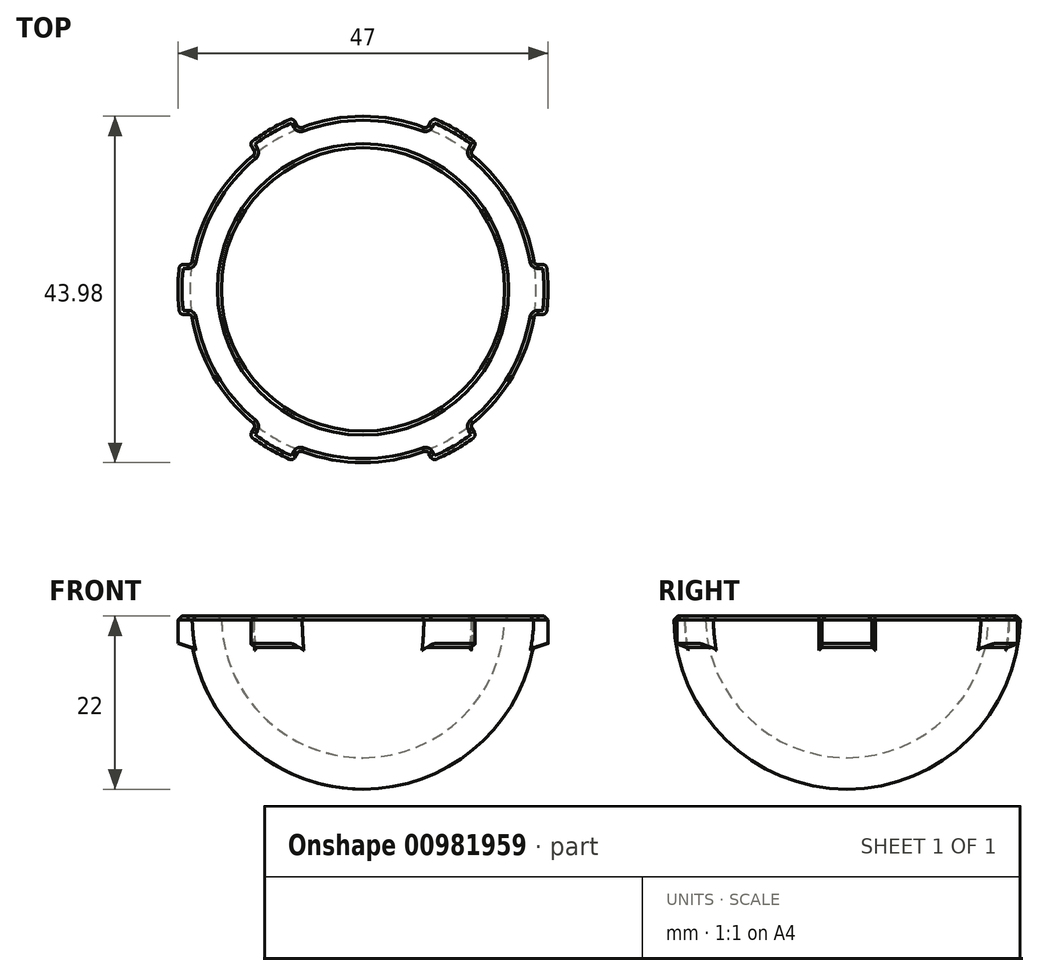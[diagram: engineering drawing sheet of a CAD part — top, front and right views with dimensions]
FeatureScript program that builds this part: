
annotation { "Feature Type Name" : "Feature", "Feature Type Description" : "" }
export const myFeature = defineFeature(function(context is Context, id is Id, definition is map)
    precondition{}
    {
        {
            var Q0;
            Q0=qCreatedBy(makeId("Front.planeOp"),FACE);
            var sketch = newSketch(context, id + "F0", { "sketchPlane" : qUnion([Q0])});
            skArc(sketch, "E0", {"start": v(-22, 0) * mm, "mid": v(-15.56, -15.56) * mm, "end": v(0, -22) * mm});
            skLineSegment(sketch, "E1", {"start": v(0, -22) * mm, "end": v(0, -18) * mm});
            skArc(sketch, "E2", {"start": v(0, -18) * mm, "mid": v(-12.73, -12.73) * mm, "end": v(-18, 0) * mm});
            skLineSegment(sketch, "E3", {"start": v(-22, 0) * mm, "end": v(-18, 0) * mm});
            skSolve(sketch);
        }
        {
            var Q0;
            Q0=makeQuery(id+"F0.imprint","IMPRINT",FACE,{"disambiguationData":[TD([[makeQuery(id+"F0.imprint","IMPRINT",EDGE,{"derivedFrom":sQuery(id+"F0.wireOp",EDGE,"E0")}),1.0]])]});
            var Q1;
            Q1=sQuery(id+"F0.wireOp",EDGE,"E1");
            revolve(context, id + "F1", {"surfaceOperationType" : NewSurfaceOperationType.NEW, "entities" : qUnion([Q0]), "axis" : qUnion([Q1]), "revolveType" : RevolveType.FULL});
        }
        {
            var Q0;
            Q0=qCreatedBy(makeId("Top.planeOp"),FACE);
            var sketch = newSketch(context, id + "F2", { "sketchPlane" : qUnion([Q0])});
            skArc(sketch, "E4", {"start": v(23.28, 3.17) * mm, "mid": v(23.5, 0) * mm, "end": v(23.28, -3.18) * mm});
            skLineSegment(sketch, "E5", {"start": v(23.28, -3.18) * mm, "end": v(18, -3.18) * mm});
            skLineSegment(sketch, "E6", {"start": v(23.28, 3.17) * mm, "end": v(18, 3.17) * mm});
            skLineSegment(sketch, "E7", {"start": v(18, 3.17) * mm, "end": v(18, -3.18) * mm});
            skSolve(sketch);
        }
        {
            var Q0;
            Q0 = qSketchRegion(id + "F2", true);
            extrude(context, id + "F3", {"entities" : qUnion([Q0]), "oppositeDirection" : true, "depth" : 4 * mm, "offsetDistance" : 25.4 * mm});
        }
        {
            var Q0;
            Q0=makeQuery(id+"F3.opExtrude","SWEPT_BODY",BODY,{"disambiguationData":[OSD([sQuery(id+"F2.wireOp",EDGE,"E4"),sQuery(id+"F2.wireOp",EDGE,"E5"),sQuery(id+"F2.wireOp",EDGE,"E6"),sQuery(id+"F2.wireOp",EDGE,"E7")])]});
            var Q1;
            Q1=sQuery(id+"F0.wireOp",EDGE,"E1");
            circularPattern(context, id + "F4", {"operationType" : NewBodyOperationType.ADD, "entities" : qUnion([Q0]), "axis" : qUnion([Q1]), "angle" : 360 * degree, "instanceCount" : 6, "equalSpace" : true});
        }
        {
            var Q0;
            Q0=makeQuery(id+"F4.opPattern","COPY",EDGE,{"derivedFrom":makeQuery(id+"F3.opExtrude","CAP_EDGE",EDGE,{"disambiguationData":[OSD([sQuery(id+"F2.wireOp",EDGE,"E4")])],"isStart":false}),"instanceName":"1"});
            var Q1;
            Q1=makeQuery(id+"F4.opPattern","COPY",EDGE,{"derivedFrom":makeQuery(id+"F3.opExtrude","CAP_EDGE",EDGE,{"disambiguationData":[OSD([sQuery(id+"F2.wireOp",EDGE,"E4")])],"isStart":false}),"instanceName":"2"});
            var Q2;
            Q2=makeQuery(id+"F3.opExtrude","CAP_EDGE",EDGE,{"disambiguationData":[OSD([sQuery(id+"F2.wireOp",EDGE,"E4")])],"isStart":false});
            var Q3;
            Q3=makeQuery(id+"F4.opPattern","COPY",EDGE,{"derivedFrom":makeQuery(id+"F3.opExtrude","CAP_EDGE",EDGE,{"disambiguationData":[OSD([sQuery(id+"F2.wireOp",EDGE,"E4")])],"isStart":false}),"instanceName":"5"});
            var Q4;
            Q4=makeQuery(id+"F4.opPattern","COPY",EDGE,{"derivedFrom":makeQuery(id+"F3.opExtrude","CAP_EDGE",EDGE,{"disambiguationData":[OSD([sQuery(id+"F2.wireOp",EDGE,"E4")])],"isStart":false}),"instanceName":"4"});
            var Q5;
            Q5=makeQuery(id+"F4.opPattern","COPY",EDGE,{"derivedFrom":makeQuery(id+"F3.opExtrude","CAP_EDGE",EDGE,{"disambiguationData":[OSD([sQuery(id+"F2.wireOp",EDGE,"E4")])],"isStart":false}),"instanceName":"3"});
            chamfer(context, id + "F5", {"entities" : qUnion([Q0, Q1, Q2, Q3, Q4, Q5]), "chamferType" : ChamferType.TWO_OFFSETS, "width1" : 0.5 * mm, "oppositeDirection" : false, "width2" : 1.52 * mm, "tangentPropagation" : true});
        }
        {
            var Q0;
            Q0=makeQuery(id+"F4.boolean.opBoolean","INTERSECT",EDGE,{"derivedFrom":[makeQuery(id+"F1.opRevolve","SWEPT_FACE",FACE,{"disambiguationData":[OSD([sQuery(id+"F0.wireOp",EDGE,"E0")])]}),makeQuery(id+"F3.opExtrude","SWEPT_FACE",FACE,{"disambiguationData":[OSD([sQuery(id+"F2.wireOp",EDGE,"E5")])]})]});
            var Q1;
            Q1=makeQuery(id+"F3.opExtrude","SWEPT_EDGE",EDGE,{"disambiguationData":[OSD([sQuery(id+"F2.wireOp",EDGE,"E4"),sQuery(id+"F2.wireOp",EDGE,"E5")])]});
            var Q2;
            Q2=makeQuery(id+"F3.opExtrude","SWEPT_EDGE",EDGE,{"disambiguationData":[OSD([sQuery(id+"F2.wireOp",EDGE,"E4"),sQuery(id+"F2.wireOp",EDGE,"E6")])]});
            var Q3;
            Q3=makeQuery(id+"F4.boolean.opBoolean","INTERSECT",EDGE,{"derivedFrom":[makeQuery(id+"F1.opRevolve","SWEPT_FACE",FACE,{"disambiguationData":[OSD([sQuery(id+"F0.wireOp",EDGE,"E0")])]}),makeQuery(id+"F3.opExtrude","SWEPT_FACE",FACE,{"disambiguationData":[OSD([sQuery(id+"F2.wireOp",EDGE,"E6")])]})]});
            var Q4;
            Q4=makeQuery(id+"F4.boolean.opBoolean","INTERSECT",EDGE,{"derivedFrom":[makeQuery(id+"F1.opRevolve","SWEPT_FACE",FACE,{"disambiguationData":[OSD([sQuery(id+"F0.wireOp",EDGE,"E0")])]}),makeQuery(id+"F4.opPattern","COPY",FACE,{"derivedFrom":makeQuery(id+"F3.opExtrude","SWEPT_FACE",FACE,{"disambiguationData":[OSD([sQuery(id+"F2.wireOp",EDGE,"E5")])]}),"instanceName":"1"})]});
            var Q5;
            Q5=makeQuery(id+"F4.opPattern","COPY",EDGE,{"derivedFrom":makeQuery(id+"F3.opExtrude","SWEPT_EDGE",EDGE,{"disambiguationData":[OSD([sQuery(id+"F2.wireOp",EDGE,"E4"),sQuery(id+"F2.wireOp",EDGE,"E5")])]}),"instanceName":"1"});
            var Q6;
            Q6=makeQuery(id+"F4.opPattern","COPY",EDGE,{"derivedFrom":makeQuery(id+"F3.opExtrude","SWEPT_EDGE",EDGE,{"disambiguationData":[OSD([sQuery(id+"F2.wireOp",EDGE,"E4"),sQuery(id+"F2.wireOp",EDGE,"E6")])]}),"instanceName":"1"});
            var Q7;
            Q7=makeQuery(id+"F4.boolean.opBoolean","INTERSECT",EDGE,{"derivedFrom":[makeQuery(id+"F1.opRevolve","SWEPT_FACE",FACE,{"disambiguationData":[OSD([sQuery(id+"F0.wireOp",EDGE,"E0")])]}),makeQuery(id+"F4.opPattern","COPY",FACE,{"derivedFrom":makeQuery(id+"F3.opExtrude","SWEPT_FACE",FACE,{"disambiguationData":[OSD([sQuery(id+"F2.wireOp",EDGE,"E6")])]}),"instanceName":"1"})]});
            var Q8;
            Q8=makeQuery(id+"F4.boolean.opBoolean","INTERSECT",EDGE,{"derivedFrom":[makeQuery(id+"F1.opRevolve","SWEPT_FACE",FACE,{"disambiguationData":[OSD([sQuery(id+"F0.wireOp",EDGE,"E0")])]}),makeQuery(id+"F4.opPattern","COPY",FACE,{"derivedFrom":makeQuery(id+"F3.opExtrude","SWEPT_FACE",FACE,{"disambiguationData":[OSD([sQuery(id+"F2.wireOp",EDGE,"E5")])]}),"instanceName":"2"})]});
            var Q9;
            Q9=makeQuery(id+"F4.opPattern","COPY",EDGE,{"derivedFrom":makeQuery(id+"F3.opExtrude","SWEPT_EDGE",EDGE,{"disambiguationData":[OSD([sQuery(id+"F2.wireOp",EDGE,"E4"),sQuery(id+"F2.wireOp",EDGE,"E5")])]}),"instanceName":"2"});
            var Q10;
            Q10=makeQuery(id+"F4.opPattern","COPY",EDGE,{"derivedFrom":makeQuery(id+"F3.opExtrude","SWEPT_EDGE",EDGE,{"disambiguationData":[OSD([sQuery(id+"F2.wireOp",EDGE,"E4"),sQuery(id+"F2.wireOp",EDGE,"E6")])]}),"instanceName":"2"});
            var Q11;
            Q11=makeQuery(id+"F4.boolean.opBoolean","INTERSECT",EDGE,{"derivedFrom":[makeQuery(id+"F1.opRevolve","SWEPT_FACE",FACE,{"disambiguationData":[OSD([sQuery(id+"F0.wireOp",EDGE,"E0")])]}),makeQuery(id+"F4.opPattern","COPY",FACE,{"derivedFrom":makeQuery(id+"F3.opExtrude","SWEPT_FACE",FACE,{"disambiguationData":[OSD([sQuery(id+"F2.wireOp",EDGE,"E6")])]}),"instanceName":"2"})]});
            var Q12;
            Q12=makeQuery(id+"F4.boolean.opBoolean","INTERSECT",EDGE,{"derivedFrom":[makeQuery(id+"F1.opRevolve","SWEPT_FACE",FACE,{"disambiguationData":[OSD([sQuery(id+"F0.wireOp",EDGE,"E0")])]}),makeQuery(id+"F4.opPattern","COPY",FACE,{"derivedFrom":makeQuery(id+"F3.opExtrude","SWEPT_FACE",FACE,{"disambiguationData":[OSD([sQuery(id+"F2.wireOp",EDGE,"E5")])]}),"instanceName":"3"})]});
            var Q13;
            Q13=makeQuery(id+"F4.opPattern","COPY",EDGE,{"derivedFrom":makeQuery(id+"F3.opExtrude","SWEPT_EDGE",EDGE,{"disambiguationData":[OSD([sQuery(id+"F2.wireOp",EDGE,"E4"),sQuery(id+"F2.wireOp",EDGE,"E5")])]}),"instanceName":"3"});
            var Q14;
            Q14=makeQuery(id+"F4.opPattern","COPY",EDGE,{"derivedFrom":makeQuery(id+"F3.opExtrude","SWEPT_EDGE",EDGE,{"disambiguationData":[OSD([sQuery(id+"F2.wireOp",EDGE,"E4"),sQuery(id+"F2.wireOp",EDGE,"E6")])]}),"instanceName":"3"});
            var Q15;
            Q15=makeQuery(id+"F4.boolean.opBoolean","INTERSECT",EDGE,{"derivedFrom":[makeQuery(id+"F1.opRevolve","SWEPT_FACE",FACE,{"disambiguationData":[OSD([sQuery(id+"F0.wireOp",EDGE,"E0")])]}),makeQuery(id+"F4.opPattern","COPY",FACE,{"derivedFrom":makeQuery(id+"F3.opExtrude","SWEPT_FACE",FACE,{"disambiguationData":[OSD([sQuery(id+"F2.wireOp",EDGE,"E6")])]}),"instanceName":"3"})]});
            var Q16;
            Q16=makeQuery(id+"F4.boolean.opBoolean","INTERSECT",EDGE,{"derivedFrom":[makeQuery(id+"F1.opRevolve","SWEPT_FACE",FACE,{"disambiguationData":[OSD([sQuery(id+"F0.wireOp",EDGE,"E0")])]}),makeQuery(id+"F4.opPattern","COPY",FACE,{"derivedFrom":makeQuery(id+"F3.opExtrude","SWEPT_FACE",FACE,{"disambiguationData":[OSD([sQuery(id+"F2.wireOp",EDGE,"E5")])]}),"instanceName":"4"})]});
            var Q17;
            Q17=makeQuery(id+"F4.opPattern","COPY",EDGE,{"derivedFrom":makeQuery(id+"F3.opExtrude","SWEPT_EDGE",EDGE,{"disambiguationData":[OSD([sQuery(id+"F2.wireOp",EDGE,"E4"),sQuery(id+"F2.wireOp",EDGE,"E5")])]}),"instanceName":"4"});
            var Q18;
            Q18=makeQuery(id+"F4.opPattern","COPY",EDGE,{"derivedFrom":makeQuery(id+"F3.opExtrude","SWEPT_EDGE",EDGE,{"disambiguationData":[OSD([sQuery(id+"F2.wireOp",EDGE,"E4"),sQuery(id+"F2.wireOp",EDGE,"E6")])]}),"instanceName":"4"});
            var Q19;
            Q19=makeQuery(id+"F4.boolean.opBoolean","INTERSECT",EDGE,{"derivedFrom":[makeQuery(id+"F1.opRevolve","SWEPT_FACE",FACE,{"disambiguationData":[OSD([sQuery(id+"F0.wireOp",EDGE,"E0")])]}),makeQuery(id+"F4.opPattern","COPY",FACE,{"derivedFrom":makeQuery(id+"F3.opExtrude","SWEPT_FACE",FACE,{"disambiguationData":[OSD([sQuery(id+"F2.wireOp",EDGE,"E6")])]}),"instanceName":"4"})]});
            var Q20;
            Q20=makeQuery(id+"F4.boolean.opBoolean","INTERSECT",EDGE,{"derivedFrom":[makeQuery(id+"F1.opRevolve","SWEPT_FACE",FACE,{"disambiguationData":[OSD([sQuery(id+"F0.wireOp",EDGE,"E0")])]}),makeQuery(id+"F4.opPattern","COPY",FACE,{"derivedFrom":makeQuery(id+"F3.opExtrude","SWEPT_FACE",FACE,{"disambiguationData":[OSD([sQuery(id+"F2.wireOp",EDGE,"E5")])]}),"instanceName":"5"})]});
            var Q21;
            Q21=makeQuery(id+"F4.opPattern","COPY",EDGE,{"derivedFrom":makeQuery(id+"F3.opExtrude","SWEPT_EDGE",EDGE,{"disambiguationData":[OSD([sQuery(id+"F2.wireOp",EDGE,"E4"),sQuery(id+"F2.wireOp",EDGE,"E5")])]}),"instanceName":"5"});
            var Q22;
            Q22=makeQuery(id+"F4.opPattern","COPY",EDGE,{"derivedFrom":makeQuery(id+"F3.opExtrude","SWEPT_EDGE",EDGE,{"disambiguationData":[OSD([sQuery(id+"F2.wireOp",EDGE,"E4"),sQuery(id+"F2.wireOp",EDGE,"E6")])]}),"instanceName":"5"});
            var Q23;
            Q23=makeQuery(id+"F4.boolean.opBoolean","INTERSECT",EDGE,{"derivedFrom":[makeQuery(id+"F1.opRevolve","SWEPT_FACE",FACE,{"disambiguationData":[OSD([sQuery(id+"F0.wireOp",EDGE,"E0")])]}),makeQuery(id+"F4.opPattern","COPY",FACE,{"derivedFrom":makeQuery(id+"F3.opExtrude","SWEPT_FACE",FACE,{"disambiguationData":[OSD([sQuery(id+"F2.wireOp",EDGE,"E6")])]}),"instanceName":"5"})]});
            var Q24;
            Q24=makeQuery(id+"F4.boolean.opBoolean","INTERSECT",EDGE,{"derivedFrom":[makeQuery(id+"F1.opRevolve","SWEPT_FACE",FACE,{"disambiguationData":[OSD([sQuery(id+"F0.wireOp",EDGE,"E0")])]}),makeQuery(id+"F4.opPattern","COPY",FACE,{"derivedFrom":makeQuery(id+"F3.opExtrude","CAP_FACE",FACE,{"disambiguationData":[OSD([sQuery(id+"F2.wireOp",EDGE,"E4"),sQuery(id+"F2.wireOp",EDGE,"E5"),sQuery(id+"F2.wireOp",EDGE,"E6"),sQuery(id+"F2.wireOp",EDGE,"E7")])],"isStart":false}),"instanceName":"5"})]});
            var Q25;
            Q25=makeQuery(id+"F4.boolean.opBoolean","INTERSECT",EDGE,{"derivedFrom":[makeQuery(id+"F1.opRevolve","SWEPT_FACE",FACE,{"disambiguationData":[OSD([sQuery(id+"F0.wireOp",EDGE,"E0")])]}),makeQuery(id+"F3.opExtrude","CAP_FACE",FACE,{"disambiguationData":[OSD([sQuery(id+"F2.wireOp",EDGE,"E4"),sQuery(id+"F2.wireOp",EDGE,"E5"),sQuery(id+"F2.wireOp",EDGE,"E6"),sQuery(id+"F2.wireOp",EDGE,"E7")])],"isStart":false})]});
            var Q26;
            Q26=makeQuery(id+"F4.boolean.opBoolean","INTERSECT",EDGE,{"derivedFrom":[makeQuery(id+"F1.opRevolve","SWEPT_FACE",FACE,{"disambiguationData":[OSD([sQuery(id+"F0.wireOp",EDGE,"E0")])]}),makeQuery(id+"F4.opPattern","COPY",FACE,{"derivedFrom":makeQuery(id+"F3.opExtrude","CAP_FACE",FACE,{"disambiguationData":[OSD([sQuery(id+"F2.wireOp",EDGE,"E4"),sQuery(id+"F2.wireOp",EDGE,"E5"),sQuery(id+"F2.wireOp",EDGE,"E6"),sQuery(id+"F2.wireOp",EDGE,"E7")])],"isStart":false}),"instanceName":"4"})]});
            var Q27;
            Q27=makeQuery(id+"F4.boolean.opBoolean","INTERSECT",EDGE,{"derivedFrom":[makeQuery(id+"F1.opRevolve","SWEPT_FACE",FACE,{"disambiguationData":[OSD([sQuery(id+"F0.wireOp",EDGE,"E0")])]}),makeQuery(id+"F4.opPattern","COPY",FACE,{"derivedFrom":makeQuery(id+"F3.opExtrude","CAP_FACE",FACE,{"disambiguationData":[OSD([sQuery(id+"F2.wireOp",EDGE,"E4"),sQuery(id+"F2.wireOp",EDGE,"E5"),sQuery(id+"F2.wireOp",EDGE,"E6"),sQuery(id+"F2.wireOp",EDGE,"E7")])],"isStart":false}),"instanceName":"3"})]});
            var Q28;
            Q28=makeQuery(id+"F4.boolean.opBoolean","INTERSECT",EDGE,{"derivedFrom":[makeQuery(id+"F1.opRevolve","SWEPT_FACE",FACE,{"disambiguationData":[OSD([sQuery(id+"F0.wireOp",EDGE,"E0")])]}),makeQuery(id+"F4.opPattern","COPY",FACE,{"derivedFrom":makeQuery(id+"F3.opExtrude","CAP_FACE",FACE,{"disambiguationData":[OSD([sQuery(id+"F2.wireOp",EDGE,"E4"),sQuery(id+"F2.wireOp",EDGE,"E5"),sQuery(id+"F2.wireOp",EDGE,"E6"),sQuery(id+"F2.wireOp",EDGE,"E7")])],"isStart":false}),"instanceName":"2"})]});
            var Q29;
            Q29=makeQuery(id+"F4.boolean.opBoolean","INTERSECT",EDGE,{"derivedFrom":[makeQuery(id+"F1.opRevolve","SWEPT_FACE",FACE,{"disambiguationData":[OSD([sQuery(id+"F0.wireOp",EDGE,"E0")])]}),makeQuery(id+"F4.opPattern","COPY",FACE,{"derivedFrom":makeQuery(id+"F3.opExtrude","CAP_FACE",FACE,{"disambiguationData":[OSD([sQuery(id+"F2.wireOp",EDGE,"E4"),sQuery(id+"F2.wireOp",EDGE,"E5"),sQuery(id+"F2.wireOp",EDGE,"E6"),sQuery(id+"F2.wireOp",EDGE,"E7")])],"isStart":false}),"instanceName":"1"})]});
            fillet(context, id + "F6", {"entities" : qUnion([Q0, Q1, Q2, Q3, Q4, Q5, Q6, Q7, Q8, Q9, Q10, Q11, Q12, Q13, Q14, Q15, Q16, Q17, Q18, Q19, Q20, Q21, Q22, Q23, Q24, Q25, Q26, Q27, Q28, Q29]), "radius" : 0.5 * mm, "tangentPropagation" : true, "allowEdgeOverflow" : false});
        }
        {
            var Q0;
            {var subQ0=sQuery(id+"F2.wireOp",EDGE,"E6");var subQ3=sQuery(id+"F0.wireOp",EDGE,"E3");var subQ4=sQuery(id+"F0.wireOp",EDGE,"E0");Q0=makeQuery(id+"F4.boolean.opBoolean","SPLIT",EDGE,{"disambiguationData":[TD([makeQuery(id+"F4.opPattern","COPY",FACE,{"derivedFrom":makeQuery(id+"F3.opExtrude","SWEPT_FACE",FACE,{"disambiguationData":[OSD([subQ0])]}),"instanceName":"4"})])],"derivedFrom":makeQuery(id+"F1.opRevolve","SWEPT_EDGE",EDGE,{"disambiguationData":[OSD([subQ4,subQ3])]})});}
            var Q1;
            Q1=makeQuery(id+"F1.opRevolve","SWEPT_EDGE",EDGE,{"disambiguationData":[OSD([sQuery(id+"F0.wireOp",EDGE,"E2"),sQuery(id+"F0.wireOp",EDGE,"E3")])]});
            chamfer(context, id + "F7", {"entities" : qUnion([Q0, Q1]), "width" : 0.5 * mm, "tangentPropagation" : true});
        }
    });
